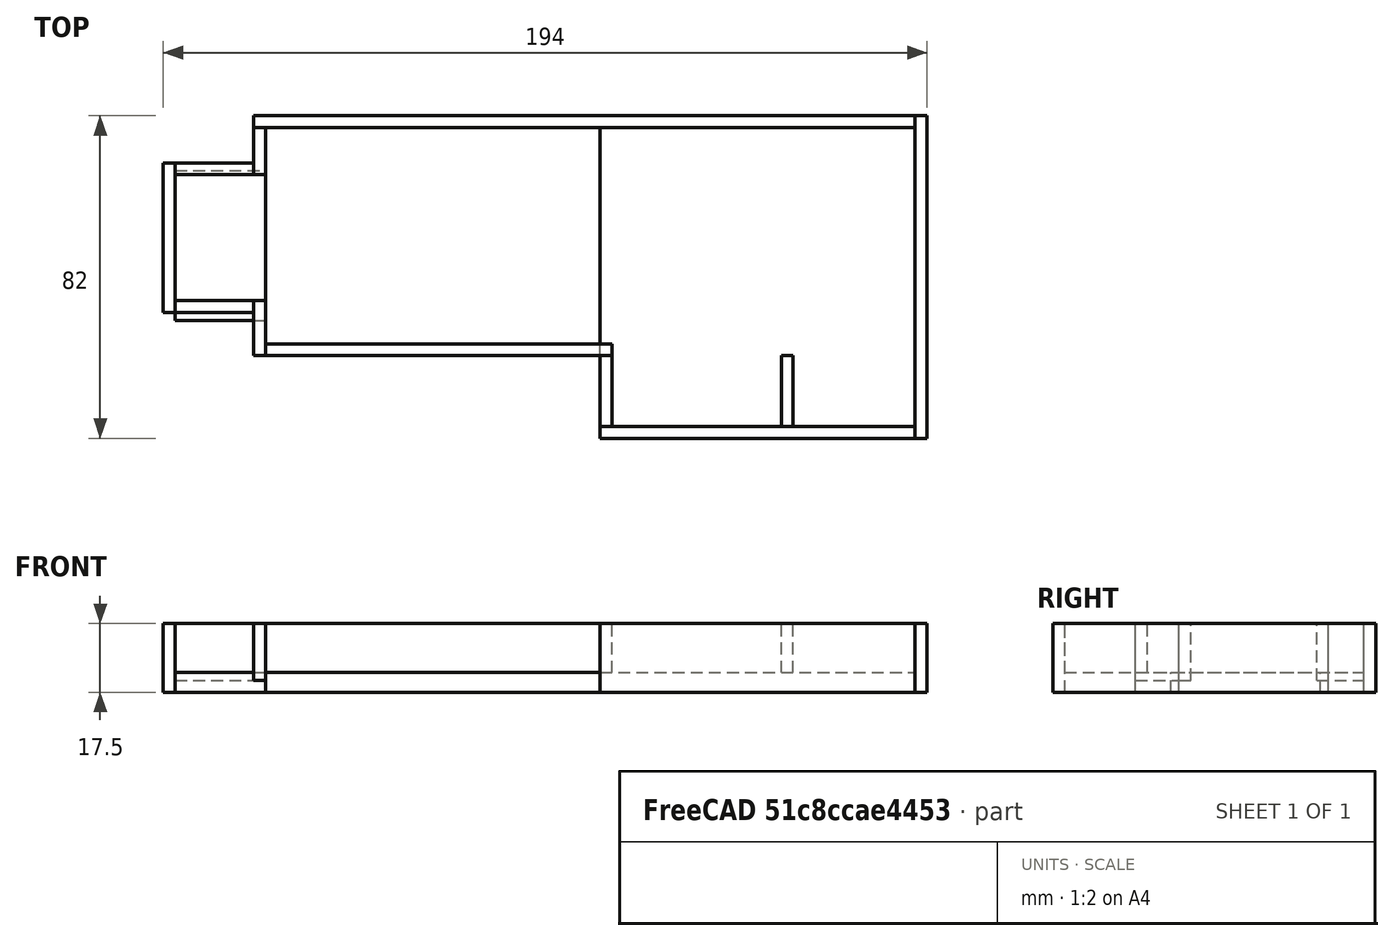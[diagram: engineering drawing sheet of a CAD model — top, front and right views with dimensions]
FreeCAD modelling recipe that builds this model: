
FCSTD DOCUMENT  (FreeCAD 0.15R4671 (Git))
Label: bread board case 23
License: All rights reserved
LicenseURL: http://en.wikipedia.org/wiki/All_rights_reserved
objects: Part::Box×14
note: 14 computed .brp shape members not serialized (recipe doc carries the construction recipe); baked Part::Feature solids carry a one-line shape summary decoded from their .brp

FEATURE [Part::Box] Box  label="base"
  Height = 5
  Length = 85
  Placement = pos=(0,18,0) rot=(0,0,1;0rad)
  Width = 58
FEATURE [Part::Box] Box001  label="platform support"
  Height = 12.5
  Length = 3
  Placement = pos=(85,0,5) rot=(0,0,1;0rad)
  Width = 18
FEATURE [Part::Box] Box004  label="side 001"
  Height = 17.5
  Length = 80
  Placement = pos=(85,-3,0) rot=(0,0,1;0rad)
  Width = 3
FEATURE [Part::Box] Box005  label="side 002"
  Height = 17.5
  Length = 168
  Placement = pos=(-3,76,0) rot=(0,0,1;0rad)
  Width = 3
FEATURE [Part::Box] Box006  label="side 003"
  Height = 14.5
  Length = 3
  Placement = pos=(-3,18,3) rot=(0,0,1;0rad)
  Width = 14
FEATURE [Part::Box] Box007  label="side 004"
  Height = 14.5
  Length = 3
  Placement = pos=(-3,64,3) rot=(0,0,1;0rad)
  Width = 12
FEATURE [Part::Box] Box008  label="side 005"
  Height = 17.5
  Length = 3
  Placement = pos=(165,-3,0) rot=(0,0,1;0rad)
  Width = 82
FEATURE [Part::Box] Box009  label="platform support001"
  Height = 12.5
  Length = 88
  Placement = pos=(0,18,5) rot=(0,0,1;0rad)
  Width = 3
FEATURE [Part::Box] Box010  label="platform support002"
  Height = 12.5
  Length = 3
  Placement = pos=(131,0,5) rot=(0,0,1;0rad)
  Width = 18
FEATURE [Part::Box] Box011  label="base 002"
  Height = 5
  Length = 23
  Placement = pos=(-23,27,0) rot=(0,0,1;0rad)
  Width = 38
FEATURE [Part::Box] Box012  label="side 006"
  Height = 14.5
  Length = 20
  Placement = pos=(-23,64,3) rot=(0,0,1;0rad)
  Width = 3
FEATURE [Part::Box] Box013  label="side 007"
  Height = 14.5
  Length = 20
  Placement = pos=(-23,29,3) rot=(0,0,1;0rad)
  Width = 3
FEATURE [Part::Box] Box014  label="side 008"
  Height = 17.5
  Length = 3
  Placement = pos=(-26,29,0) rot=(0,0,1;0rad)
  Width = 38
FEATURE [Part::Box] Box015  label="base001"
  Height = 5
  Length = 80
  Placement = pos=(85,0,0) rot=(0,0,1;0rad)
  Width = 76
